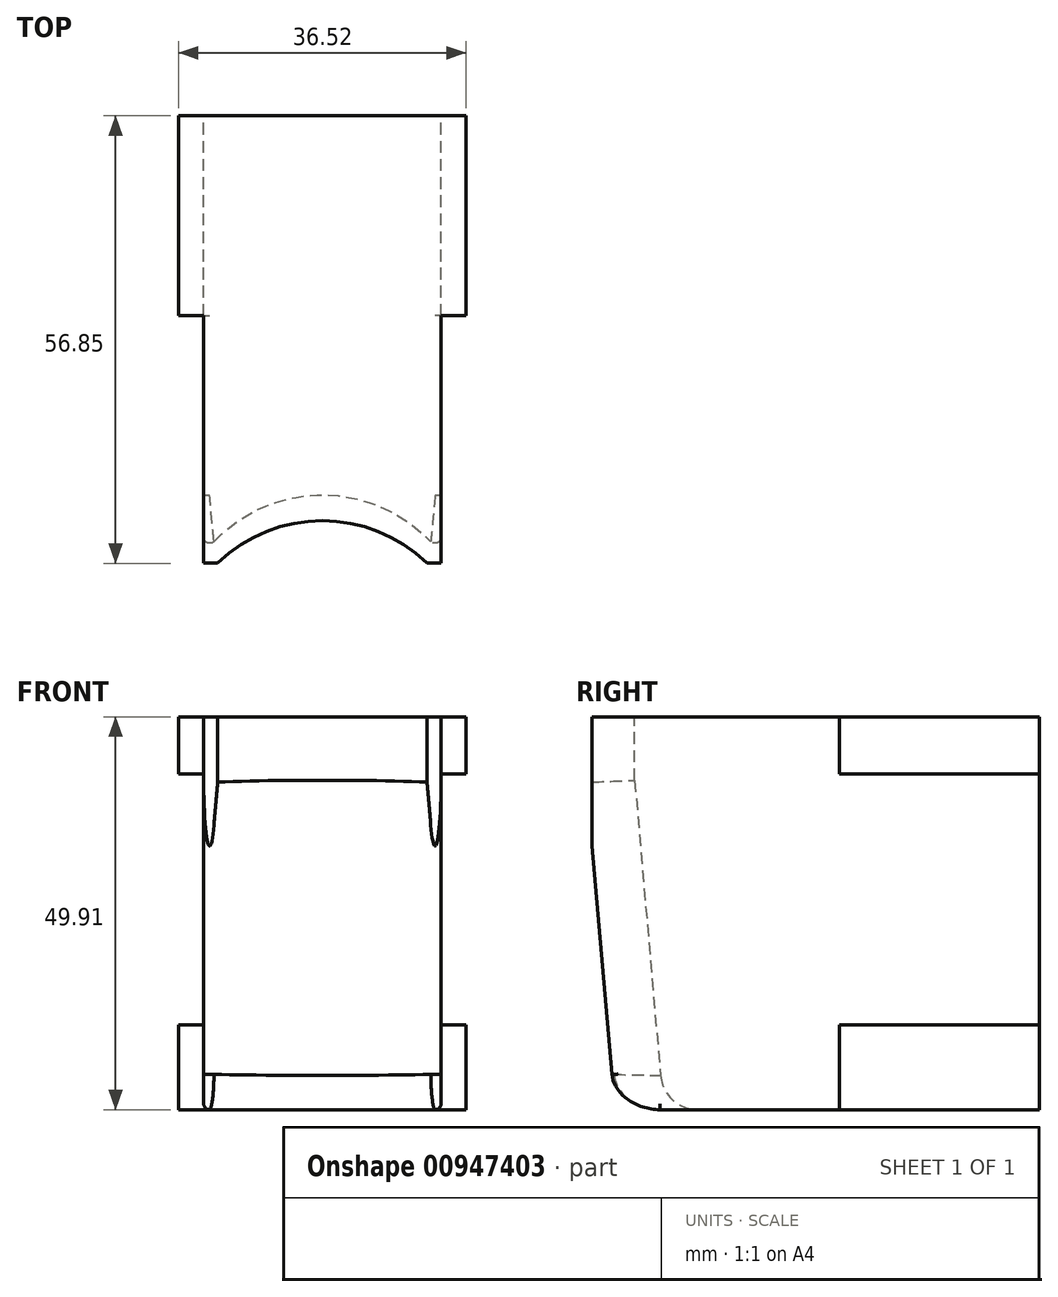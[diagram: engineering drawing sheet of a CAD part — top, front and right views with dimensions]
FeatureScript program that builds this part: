
annotation { "Feature Type Name" : "Feature", "Feature Type Description" : "" }
export const myFeature = defineFeature(function(context is Context, id is Id, definition is map)
    precondition{}
    {
        {
            var Q0;
            Q0=qCreatedBy(makeId("Front.planeOp"),FACE);
            cPlane(context, id + "F0", {"entities" : qUnion([Q0]), "cplaneType" : CPlaneType.OFFSET, "offset" : 70.48 * mm, "width" : 152.4 * mm, "height" : 152.4 * mm});
        }
        {
            var Q0;
            Q0=qCreatedBy(makeId("Top.planeOp"),FACE);
            var sketch = newSketch(context, id + "F1", { "sketchPlane" : qUnion([Q0])});
            skLineSegment(sketch, "E0.bottom", {"start": v(-18.26, 0) * mm, "end": v(18.26, 0) * mm});
            skLineSegment(sketch, "E0.top", {"start": v(-18.26, -56.85) * mm, "end": v(18.26, -56.85) * mm});
            skLineSegment(sketch, "E0.left", {"start": v(-18.26, 0) * mm, "end": v(-18.26, -56.85) * mm});
            skLineSegment(sketch, "E0.right", {"start": v(18.26, 0) * mm, "end": v(18.26, -56.85) * mm});
            skLineSegment(sketch, "E1", {"start": v(0, 0) * mm, "end": v(0, 47.51) * mm, "construction": true});
            skSolve(sketch);
        }
        {
            var Q0;
            Q0=qSketchRegion(id+"F1",true);
            extrude(context, id + "F2", {"entities" : qUnion([Q0]), "oppositeDirection" : true, "depth" : 49.9 * mm, "offsetDistance" : 25.4 * mm});
        }
        {
            var Q0;
            Q0=makeQuery(id+"F2.opExtrude","CAP_FACE",FACE,{"disambiguationData":[OSD([sQuery(id+"F1.wireOp",EDGE,"E0.bottom"),sQuery(id+"F1.wireOp",EDGE,"E0.top"),sQuery(id+"F1.wireOp",EDGE,"E0.left"),sQuery(id+"F1.wireOp",EDGE,"E0.right")])],"isStart":true});
            var sketch = newSketch(context, id + "F3", { "sketchPlane" : qUnion([Q0])});
            skLineSegment(sketch, "E2", {"start": v(0, 19.2) * mm, "end": v(0, -55.36) * mm, "construction": true});
            skLineSegment(sketch, "E3.bottom", {"start": v(-18.26, -25.4) * mm, "end": v(-15.08, -25.4) * mm});
            skLineSegment(sketch, "E3.top", {"start": v(-18.26, -56.85) * mm, "end": v(-15.08, -56.85) * mm});
            skLineSegment(sketch, "E3.left", {"start": v(-18.26, -25.4) * mm, "end": v(-18.26, -56.85) * mm});
            skLineSegment(sketch, "E3.right", {"start": v(-15.08, -25.4) * mm, "end": v(-15.08, -56.85) * mm});
            skLineSegment(sketch, "E4.MirrorCS", {"start": v(18.26, -56.85) * mm, "end": v(15.08, -56.85) * mm});
            skLineSegment(sketch, "E5.MirrorCS", {"start": v(15.08, -25.4) * mm, "end": v(15.08, -56.85) * mm});
            skLineSegment(sketch, "E6.MirrorCS", {"start": v(18.26, -25.4) * mm, "end": v(18.26, -56.85) * mm});
            skLineSegment(sketch, "E7.MirrorCS", {"start": v(18.26, -25.4) * mm, "end": v(15.08, -25.4) * mm});
            skSolve(sketch);
        }
        {
            var Q0;
            Q0=qSketchRegion(id+"F3",true);
            extrude(context, id + "F4", {"entities" : qUnion([Q0]), "operationType" : NewBodyOperationType.REMOVE, "endBound" : BoundingType.THROUGH_ALL, "oppositeDirection" : true, "depth" : 25.4 * mm, "offsetDistance" : 25.4 * mm});
        }
        {
            var Q0;
            Q0=makeQuery(id+"F2.opExtrude","CAP_FACE",FACE,{"disambiguationData":[OSD([sQuery(id+"F1.wireOp",EDGE,"E0.bottom"),sQuery(id+"F1.wireOp",EDGE,"E0.top"),sQuery(id+"F1.wireOp",EDGE,"E0.left"),sQuery(id+"F1.wireOp",EDGE,"E0.right")])],"isStart":true});
            var sketch = newSketch(context, id + "F5", { "sketchPlane" : qUnion([Q0])});
            skCircle(sketch, "E8", {"center": v(0, -70.48) * mm, "radius": 19.05 * mm});
            skSolve(sketch);
        }
        {
            var Q0;
            Q0=qSketchRegion(id+"F5",true);
            extrude(context, id + "F6", {"entities" : qUnion([Q0]), "operationType" : NewBodyOperationType.REMOVE, "endBound" : BoundingType.THROUGH_ALL, "oppositeDirection" : true, "depth" : 25.4 * mm, "offsetDistance" : 25.4 * mm});
        }
        {
            var Q0;
            Q0=makeQuery(id+"F2.opExtrude","SWEPT_FACE",FACE,{"disambiguationData":[OSD([sQuery(id+"F1.wireOp",EDGE,"E0.bottom")])]});
            var sketch = newSketch(context, id + "F7", { "sketchPlane" : qUnion([Q0])});
            skLineSegment(sketch, "E9", {"start": v(0, 25.85) * mm, "end": v(0, -64.06) * mm, "construction": true});
            skLineSegment(sketch, "E10.bottom", {"start": v(-18.26, -7.24) * mm, "end": v(-15.08, -7.24) * mm});
            skLineSegment(sketch, "E10.top", {"start": v(-18.26, -39.12) * mm, "end": v(-15.08, -39.12) * mm});
            skLineSegment(sketch, "E10.left", {"start": v(-18.26, -7.24) * mm, "end": v(-18.26, -39.12) * mm});
            skLineSegment(sketch, "E10.right", {"start": v(-15.08, -7.24) * mm, "end": v(-15.08, -39.12) * mm});
            skLineSegment(sketch, "E11.MirrorCS", {"start": v(18.26, -7.24) * mm, "end": v(18.26, -39.12) * mm});
            skLineSegment(sketch, "E12.MirrorCS", {"start": v(15.08, -7.24) * mm, "end": v(15.08, -39.12) * mm});
            skLineSegment(sketch, "E13.MirrorCS", {"start": v(18.26, -7.24) * mm, "end": v(15.08, -7.24) * mm});
            skLineSegment(sketch, "E14.MirrorCS", {"start": v(18.26, -39.12) * mm, "end": v(15.08, -39.12) * mm});
            skSolve(sketch);
        }
        {
            var Q0;
            Q0=qSketchRegion(id+"F7",true);
            extrude(context, id + "F8", {"entities" : qUnion([Q0]), "operationType" : NewBodyOperationType.REMOVE, "endBound" : BoundingType.THROUGH_ALL, "oppositeDirection" : true, "depth" : 25.4 * mm, "offsetDistance" : 25.4 * mm});
        }
        {
            var Q0;
            Q0=qCreatedBy(makeId("Right.planeOp"),FACE);
            var sketch = newSketch(context, id + "F9", { "sketchPlane" : qUnion([Q0])});
            skLineSegment(sketch, "E15", {"start": v(-70.48, -8.89) * mm, "end": v(-66.34, -56.26) * mm, "construction": true});
            skLineSegment(sketch, "E16.left", {"start": v(-71.26, 0) * mm, "end": v(-66.34, -56.26) * mm});
            skLineSegment(sketch, "E16.right", {"start": v(-52.29, 1.66) * mm, "end": v(-47.36, -54.6) * mm});
            skLineSegment(sketch, "E17", {"start": v(-71.26, 0) * mm, "end": v(-52.29, 1.66) * mm});
            skLineSegment(sketch, "E18", {"start": v(-66.34, -56.26) * mm, "end": v(-47.36, -54.6) * mm});
            skSolve(sketch);
        }
        {
            var Q0;
            Q0 = qSketchRegion(id + "F9", true);
            var Q1;
            Q1=sQuery(id+"F9.wireOp",EDGE,"E16.left");
            revolve(context, id + "F10", {"operationType" : NewBodyOperationType.REMOVE, "surfaceOperationType" : NewSurfaceOperationType.NEW, "entities" : qUnion([Q0]), "axis" : qUnion([Q1]), "revolveType" : RevolveType.FULL, "oppositeDirection" : true});
        }
        {
            var Q0;
            Q0=makeQuery(id+"F10.boolean.opBoolean","INTERSECT",EDGE,{"derivedFrom":[makeQuery(id+"F2.opExtrude","CAP_FACE",FACE,{"disambiguationData":[OSD([sQuery(id+"F1.wireOp",EDGE,"E0.bottom"),sQuery(id+"F1.wireOp",EDGE,"E0.top"),sQuery(id+"F1.wireOp",EDGE,"E0.left"),sQuery(id+"F1.wireOp",EDGE,"E0.right")])],"isStart":false}),makeQuery(id+"F10.opRevolve","SWEPT_FACE",FACE,{"disambiguationData":[OSD([sQuery(id+"F9.wireOp",EDGE,"E16.right")])]})]});
            fillet(context, id + "F11", {"entities" : qUnion([Q0]), "radius" : 4.76 * mm, "tangentPropagation" : true, "allowEdgeOverflow" : false});
        }
        {
            var Q0;
            Q0=makeQuery(id+"F10.boolean.opBoolean","INTERSECT",EDGE,{"derivedFrom":[makeQuery(id+"F8.boolean.opBoolean","MERGE",FACE,{"derivedFrom":[makeQuery(id+"F4.boolean.opBoolean","COPY",FACE,{"derivedFrom":makeQuery(id+"F4.opExtrude","SWEPT_FACE",FACE,{"disambiguationData":[OSD([sQuery(id+"F3.wireOp",EDGE,"E5.MirrorCS")])]})})],"fromTools":[makeQuery(id+"F8.opExtrude","SWEPT_FACE",FACE,{"disambiguationData":[OSD([sQuery(id+"F7.wireOp",EDGE,"E10.right")])]})]}),makeQuery(id+"F10.opRevolve","SWEPT_FACE",FACE,{"disambiguationData":[OSD([sQuery(id+"F9.wireOp",EDGE,"E16.right")])]})]});
            var Q1;
            Q1=makeQuery(id+"F10.boolean.opBoolean","INTERSECT",EDGE,{"derivedFrom":[makeQuery(id+"F8.boolean.opBoolean","MERGE",FACE,{"derivedFrom":[makeQuery(id+"F4.boolean.opBoolean","COPY",FACE,{"derivedFrom":makeQuery(id+"F4.opExtrude","SWEPT_FACE",FACE,{"disambiguationData":[OSD([sQuery(id+"F3.wireOp",EDGE,"E3.right")])]})})],"fromTools":[makeQuery(id+"F8.opExtrude","SWEPT_FACE",FACE,{"disambiguationData":[OSD([sQuery(id+"F7.wireOp",EDGE,"E12.MirrorCS")])]})]}),makeQuery(id+"F10.opRevolve","SWEPT_FACE",FACE,{"disambiguationData":[OSD([sQuery(id+"F9.wireOp",EDGE,"E16.right")])]})]});
            fillet(context, id + "F12", {"entities" : qUnion([Q0, Q1]), "radius" : 0.76 * mm, "tangentPropagation" : true, "allowEdgeOverflow" : false});
        }
    });
